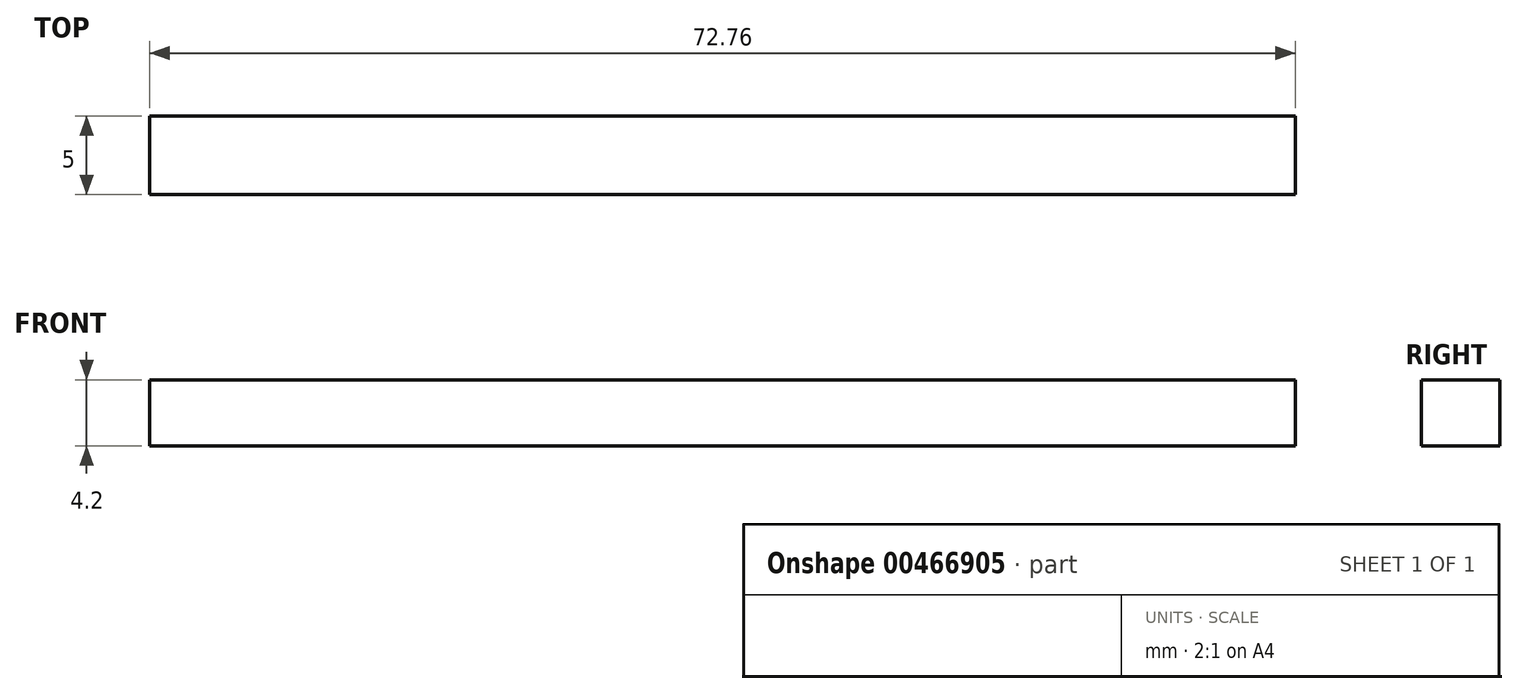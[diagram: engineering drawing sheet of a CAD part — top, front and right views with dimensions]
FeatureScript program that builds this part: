
annotation { "Feature Type Name" : "Feature", "Feature Type Description" : "" }
export const myFeature = defineFeature(function(context is Context, id is Id, definition is map)
    precondition{}
    {
        {
            var Q0;
            Q0=qCreatedBy(makeId("Top.planeOp"),FACE);
            var sketch = newSketch(context, id + "F0", { "sketchPlane" : qUnion([Q0])});
            skLineSegment(sketch, "E0.bottom", {"start": v(-36.38, -2.5) * mm, "end": v(36.38, -2.5) * mm});
            skLineSegment(sketch, "E0.top", {"start": v(-36.38, 2.5) * mm, "end": v(36.38, 2.5) * mm});
            skLineSegment(sketch, "E0.left", {"start": v(-36.38, -2.5) * mm, "end": v(-36.38, 2.5) * mm});
            skLineSegment(sketch, "E0.right", {"start": v(36.38, -2.5) * mm, "end": v(36.38, 2.5) * mm});
            skPoint(sketch, "E0.middle", {"position": v(0, 0) * mm});
            skSolve(sketch);
        }
        {
            var Q0;
            Q0 = qSketchRegion(id + "F0", true);
            extrude(context, id + "F1", {"entities" : qUnion([Q0]), "depth" : 4.2 * mm});
        }
    });
